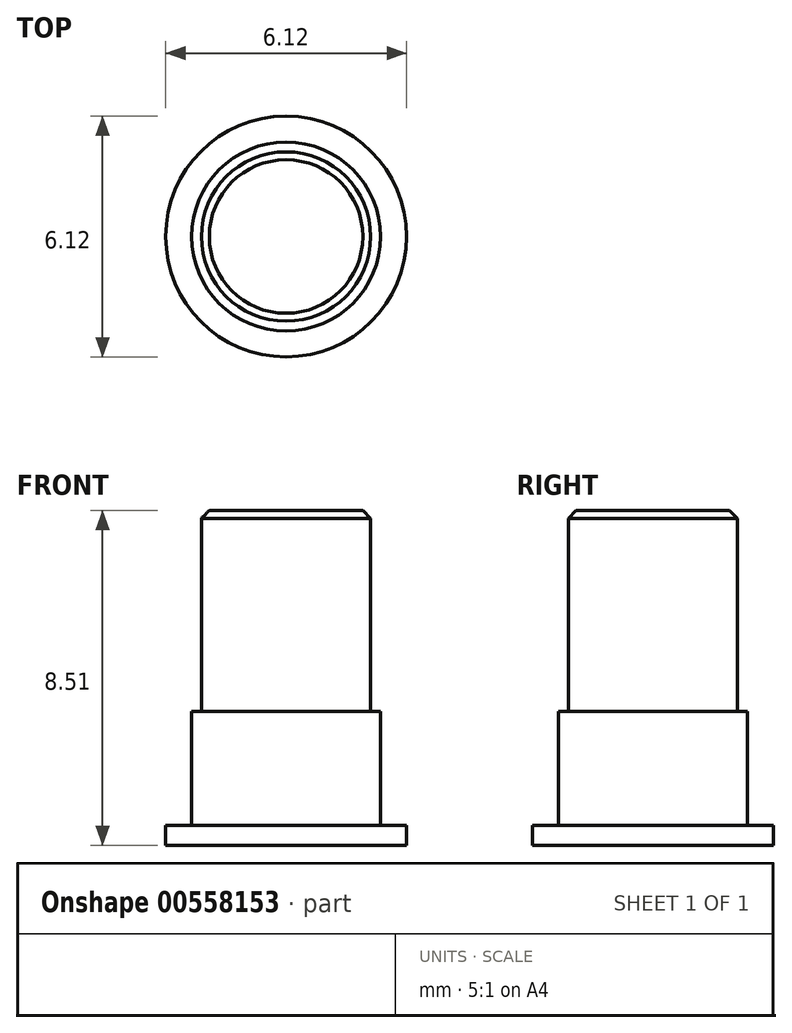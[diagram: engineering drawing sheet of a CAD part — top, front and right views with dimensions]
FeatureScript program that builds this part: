
annotation { "Feature Type Name" : "Feature", "Feature Type Description" : "" }
export const myFeature = defineFeature(function(context is Context, id is Id, definition is map)
    precondition{}
    {
        {
            var Q0;
            Q0=qCreatedBy(makeId("Front.planeOp"),FACE);
            var sketch = newSketch(context, id + "F0", { "sketchPlane" : qUnion([Q0])});
            skLineSegment(sketch, "E0", {"start": v(2.4, 0) * mm, "end": v(2.4, 2.9) * mm});
            skLineSegment(sketch, "E1", {"start": v(2.15, 4.5) * mm, "end": v(2.15, 8) * mm});
            skLineSegment(sketch, "E2", {"start": v(2.15, 8) * mm, "end": v(0, 8) * mm});
            skPoint(sketch, "E3.end.orphan", {"position": v(0, 0.5) * mm});
            skPoint(sketch, "E4.end.orphan", {"position": v(1.5, 0.5) * mm});
            skLineSegment(sketch, "E5", {"start": v(2.4, 2.9) * mm, "end": v(2.15, 2.9) * mm});
            skLineSegment(sketch, "E6", {"start": v(2.15, 4.5) * mm, "end": v(2.15, 2.9) * mm});
            skPoint(sketch, "E6.endSnap0", {"position": v(2.4, 2.5) * mm});
            skPoint(sketch, "E7.orphan", {"position": v(2.15, 2.5) * mm});
            skPoint(sketch, "E8.start.orphan", {"position": v(2.4, 5.51) * mm});
            skPoint(sketch, "E9.orphan", {"position": v(2.4, -0.5) * mm});
            skLineSegment(sketch, "E10", {"start": v(3.06, -0.5) * mm, "end": v(0, -0.5) * mm});
            skPoint(sketch, "E11.end.orphan", {"position": v(0, 0) * mm});
            skPoint(sketch, "E12.end.orphan", {"position": v(3, 0) * mm});
            skPoint(sketch, "E13.end.orphan", {"position": v(3.06, 0) * mm});
            skLineSegment(sketch, "E14", {"start": v(3.06, -0.5) * mm, "end": v(3.06, 0) * mm});
            skLineSegment(sketch, "E15", {"start": v(3.06, 0) * mm, "end": v(2.4, 0) * mm});
            skLineSegment(sketch, "E16", {"start": v(2.4, 0) * mm, "end": v(3.06, 0) * mm});
            skLineSegment(sketch, "E17", {"start": v(0, 8) * mm, "end": v(0, -0.5) * mm});
            skSolve(sketch);
        }
        {
            var Q0;
            Q0=makeQuery(id+"F0.imprint","IMPRINT",FACE,{"disambiguationData":[TD([[makeQuery(id+"F0.imprint","IMPRINT",EDGE,{"derivedFrom":sQuery(id+"F0.wireOp",EDGE,"E0")}),1.0]])]});
            var Q1;
            Q1=sQuery(id+"F0.wireOp",EDGE,"E17");
            revolve(context, id + "F1", {"entities" : qUnion([Q0]), "axis" : qUnion([Q1]), "revolveType" : RevolveType.FULL});
        }
        {
            var Q0;
            Q0=makeQuery(id+"F1.opRevolve","SWEPT_EDGE",EDGE,{"disambiguationData":[OSD([sQuery(id+"F0.wireOp",EDGE,"E1"),sQuery(id+"F0.wireOp",EDGE,"E2")])]});
            chamfer(context, id + "F2", {"entities" : qUnion([Q0]), "width" : 0.2 * mm, "tangentPropagation" : true});
        }
    });
